# Revit family: Sink-Top_Undermount-Kitchen-KOHLER-Cairn-K-27815T
name_source: partatom
category: Plumbing Fixtures
units: mm (PartAtom-declared; Revit-internal decimal feet)

## family parameters
Cut with Voids When Loaded = No
Host = Face
OmniClass Number = 23.31.13.00
OmniClass Title = Sinks
Part Type = Normal
Room Calculation Point = No
Round Connector Dimension = Use Diameter
Shared = No

## types (3) — shared parameters
ADA Compliant = No
Assembly Code = D2010400
CW Connection = No
Cold Water Inlet = Cold Water Inlet
Date Modified = 02/28/2023
Default Elevation = 36"
Description = Sized Trough Table On The Upper And Lower Counters Double Kitchen Basin, Starry Sky Black
Drain Included = Yes
HW Connection = No
Height = 9 5/8"
Hot Water Inlet = Hot Water Inlet
Length = 33 1/16"
Manufacturer = Kohler Co.
Master Format 2014 = 22 41 16
Master Format 2014 Name = Residential Lavatories and Sinks
Material = Neoroc
Product Name = Cairn
URL = http://www.kohler.com.cn
Vent Connection = No
Waste Connection = Yes
Waste Water Outlet 1 = Waste Water Outlet 1
Waste Water Outlet 2 = Waste Water Outlet 2
WaterSense Certified = No
Width = 18 1/2"

## per-type parameters (varying)
| type | Finish | Model | Product Documentation Link | Product Page URL | Type |
| CM3-Matte Taupe | Kohler-Neoroc-CM3-Matte_Taupe | K-27815T-2HD-CM3 |  |  | 1 |
| CM6-Matte White | KOHLER-Neoroc-CM6-Matte_White | K-27815T-2HD-CM6 |  |  | 2 |
| UM1-Star Black | Kohler-Neoroc-UM1-Star_Black | K-27815T-2HD-UM1 | https://files.kohler.com.cn | https://www.kohler.com.cn | 3 |

## geometry (parser evidence)
native form markers: Sweep x10
no freeform markers — native parametric forms only
